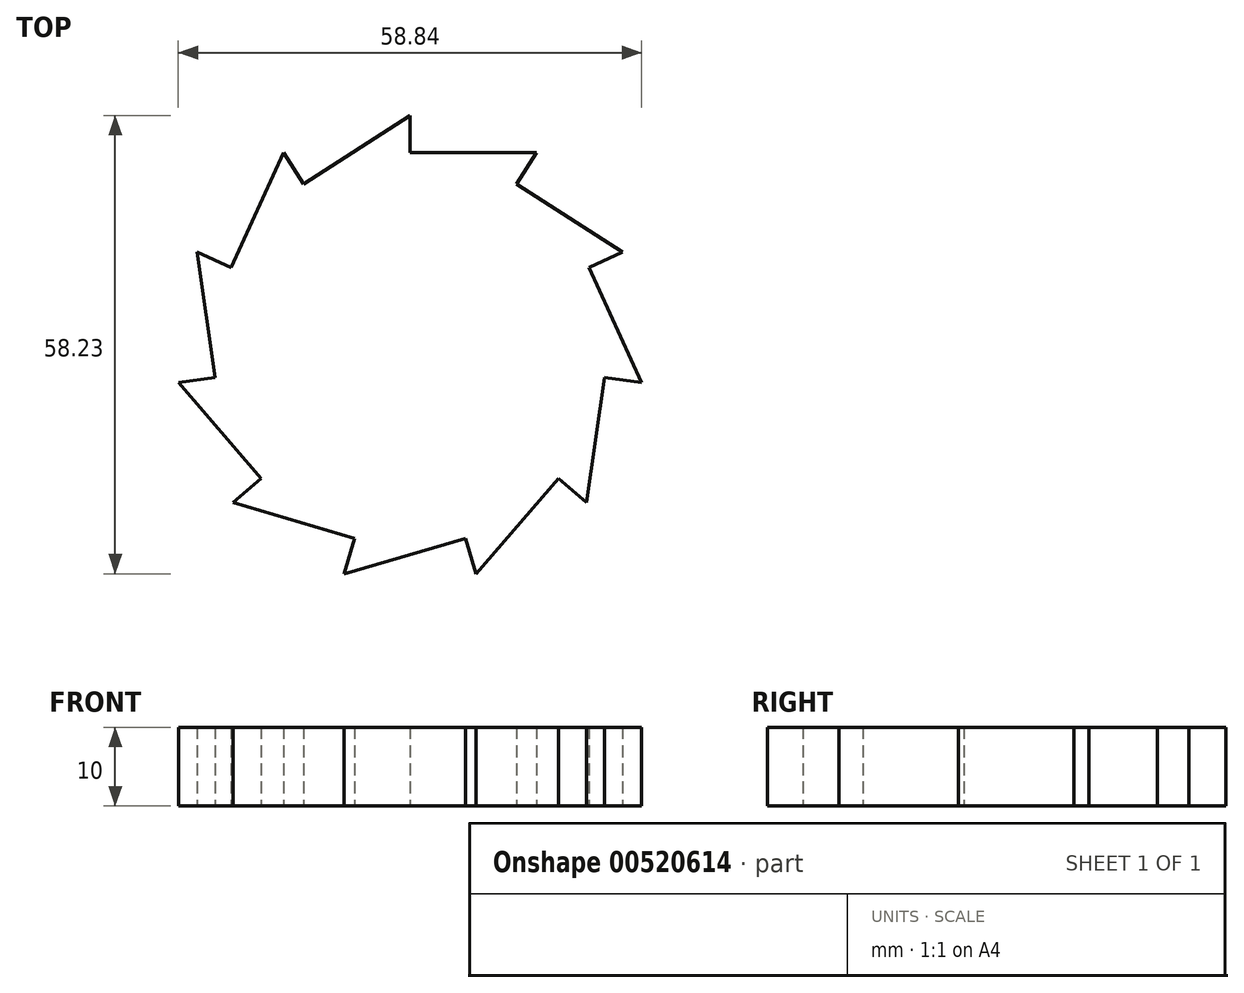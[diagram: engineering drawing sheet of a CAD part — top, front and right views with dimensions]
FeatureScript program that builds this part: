
annotation { "Feature Type Name" : "Feature", "Feature Type Description" : "" }
export const myFeature = defineFeature(function(context is Context, id is Id, definition is map)
    precondition{}
    {
        {
            var Q0;
            Q0=qCreatedBy(makeId("Top.planeOp"),FACE);
            var sketch = newSketch(context, id + "F0", { "sketchPlane" : qUnion([Q0])});
            skArc(sketch, "E0", {"start": v(0.43, 30) * mm, "mid": v(0.22, 30) * mm, "end": v(0, 30) * mm});
            skLineSegment(sketch, "E1", {"start": v(0, 30) * mm, "end": v(0, 25) * mm});
            skLineSegment(sketch, "E2", {"start": v(0, 25) * mm, "end": v(16.58, 25) * mm});
            skLineSegment(sketch, "E3.1.0", {"start": v(-16.22, 25.24) * mm, "end": v(-13.52, 21.03) * mm});
            skLineSegment(sketch, "E3.1.1", {"start": v(-13.52, 21.03) * mm, "end": v(0.43, 30) * mm});
            skLineSegment(sketch, "E3.2.0", {"start": v(-27.29, 12.46) * mm, "end": v(-22.74, 10.39) * mm});
            skLineSegment(sketch, "E3.2.1", {"start": v(-22.74, 10.39) * mm, "end": v(-15.85, 25.47) * mm});
            skLineSegment(sketch, "E3.3.0", {"start": v(-29.7, -4.27) * mm, "end": v(-24.75, -3.56) * mm});
            skLineSegment(sketch, "E3.3.1", {"start": v(-24.75, -3.56) * mm, "end": v(-27.1, 12.86) * mm});
            skLineSegment(sketch, "E3.4.0", {"start": v(-22.67, -19.65) * mm, "end": v(-18.9, -16.37) * mm});
            skLineSegment(sketch, "E3.4.1", {"start": v(-18.9, -16.37) * mm, "end": v(-29.75, -3.84) * mm});
            skLineSegment(sketch, "E3.5.0", {"start": v(-8.45, -28.78) * mm, "end": v(-7.04, -23.99) * mm});
            skLineSegment(sketch, "E3.5.1", {"start": v(-7.04, -23.99) * mm, "end": v(-22.95, -19.32) * mm});
            skLineSegment(sketch, "E3.6.0", {"start": v(8.45, -28.78) * mm, "end": v(7.04, -23.99) * mm});
            skLineSegment(sketch, "E3.6.1", {"start": v(7.04, -23.99) * mm, "end": v(-8.87, -28.66) * mm});
            skLineSegment(sketch, "E3.7.0", {"start": v(22.67, -19.65) * mm, "end": v(18.9, -16.37) * mm});
            skLineSegment(sketch, "E3.7.1", {"start": v(18.9, -16.37) * mm, "end": v(8.03, -28.9) * mm});
            skLineSegment(sketch, "E3.8.0", {"start": v(29.7, -4.27) * mm, "end": v(24.75, -3.56) * mm});
            skLineSegment(sketch, "E3.8.1", {"start": v(24.75, -3.56) * mm, "end": v(22.39, -19.97) * mm});
            skLineSegment(sketch, "E3.9.0", {"start": v(27.29, 12.46) * mm, "end": v(22.74, 10.39) * mm});
            skLineSegment(sketch, "E3.9.1", {"start": v(22.74, 10.39) * mm, "end": v(29.63, -4.7) * mm});
            skLineSegment(sketch, "E3.10.0", {"start": v(16.22, 25.24) * mm, "end": v(13.52, 21.03) * mm});
            skLineSegment(sketch, "E3.10.1", {"start": v(13.52, 21.03) * mm, "end": v(27.47, 12.07) * mm});
            skArc(sketch, "E4.trimOffspring", {"start": v(16.58, 25) * mm, "mid": v(16.4, 25.12) * mm, "end": v(16.22, 25.24) * mm});
            skArc(sketch, "E5.trimOffspring", {"start": v(27.47, 12.07) * mm, "mid": v(27.38, 12.26) * mm, "end": v(27.29, 12.46) * mm});
            skArc(sketch, "E6.trimOffspring", {"start": v(29.63, -4.7) * mm, "mid": v(29.66, -4.48) * mm, "end": v(29.7, -4.27) * mm});
            skArc(sketch, "E7.trimOffspring", {"start": v(22.39, -19.97) * mm, "mid": v(22.53, -19.8) * mm, "end": v(22.67, -19.65) * mm});
            skArc(sketch, "E8.trimOffspring", {"start": v(8.03, -28.9) * mm, "mid": v(8.24, -28.85) * mm, "end": v(8.45, -28.78) * mm});
            skArc(sketch, "E9.trimOffspring", {"start": v(-8.87, -28.66) * mm, "mid": v(-8.66, -28.72) * mm, "end": v(-8.45, -28.78) * mm});
            skArc(sketch, "E10.trimOffspring", {"start": v(-22.95, -19.32) * mm, "mid": v(-22.81, -19.48) * mm, "end": v(-22.67, -19.65) * mm});
            skArc(sketch, "E11.trimOffspring", {"start": v(-29.75, -3.84) * mm, "mid": v(-29.72, -4.05) * mm, "end": v(-29.7, -4.27) * mm});
            skArc(sketch, "E12.trimOffspring", {"start": v(-27.1, 12.86) * mm, "mid": v(-27.2, 12.66) * mm, "end": v(-27.29, 12.46) * mm});
            skArc(sketch, "E13.trimOffspring", {"start": v(-15.85, 25.47) * mm, "mid": v(-16.04, 25.35) * mm, "end": v(-16.22, 25.24) * mm});
            skSolve(sketch);
        }
        {
            var Q0;
            {var subQ8=sQuery(id+"F0.wireOp",EDGE,"E2");var subQ26=sQuery(id+"F0.wireOp",EDGE,"E1");var subQ27=makeQuery(id+"F0.imprint","INTERSECT",VERTEX,{"derivedFrom":[subQ26,subQ8]});Q0=makeQuery(id+"F0.imprint","IMPRINT",FACE,{"disambiguationData":[TD([[makeQuery(id+"F0.imprint","IMPRINT",EDGE,{"disambiguationData":[TD([[subQ27,1.0]])],"derivedFrom":subQ26}),-1.0]])]});}
            extrude(context, id + "F1", {"entities" : qUnion([Q0]), "depth" : 10 * mm, "offsetDistance" : 25 * mm});
        }
    });
